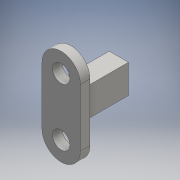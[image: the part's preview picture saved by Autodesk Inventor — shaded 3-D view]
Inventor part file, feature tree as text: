
AUTODESK INVENTOR PART (.ipt)
format: ipt  version: 2016 (Build 200138000, 138)  size: 117,760 bytes
history: native  units: mm
features: extrude x2, sketch x2, other x1
ambient origin geometry x8: Origin, YZ Plane, XZ Plane, XY Plane, X Axis, Y Axis, Z Axis, Center Point
bodies: Body1 (feature_tree)
feature tree (5):
  other  "Bryła1"
  extrude  "Wyciągnięcie proste1"  Depth=9.0mm
  extrude  "Wyciągnięcie proste2"  Depth=5.0mm TaperAngle=0.0deg
  sketch  "Szkic1"
  sketch  "Szkic2"
